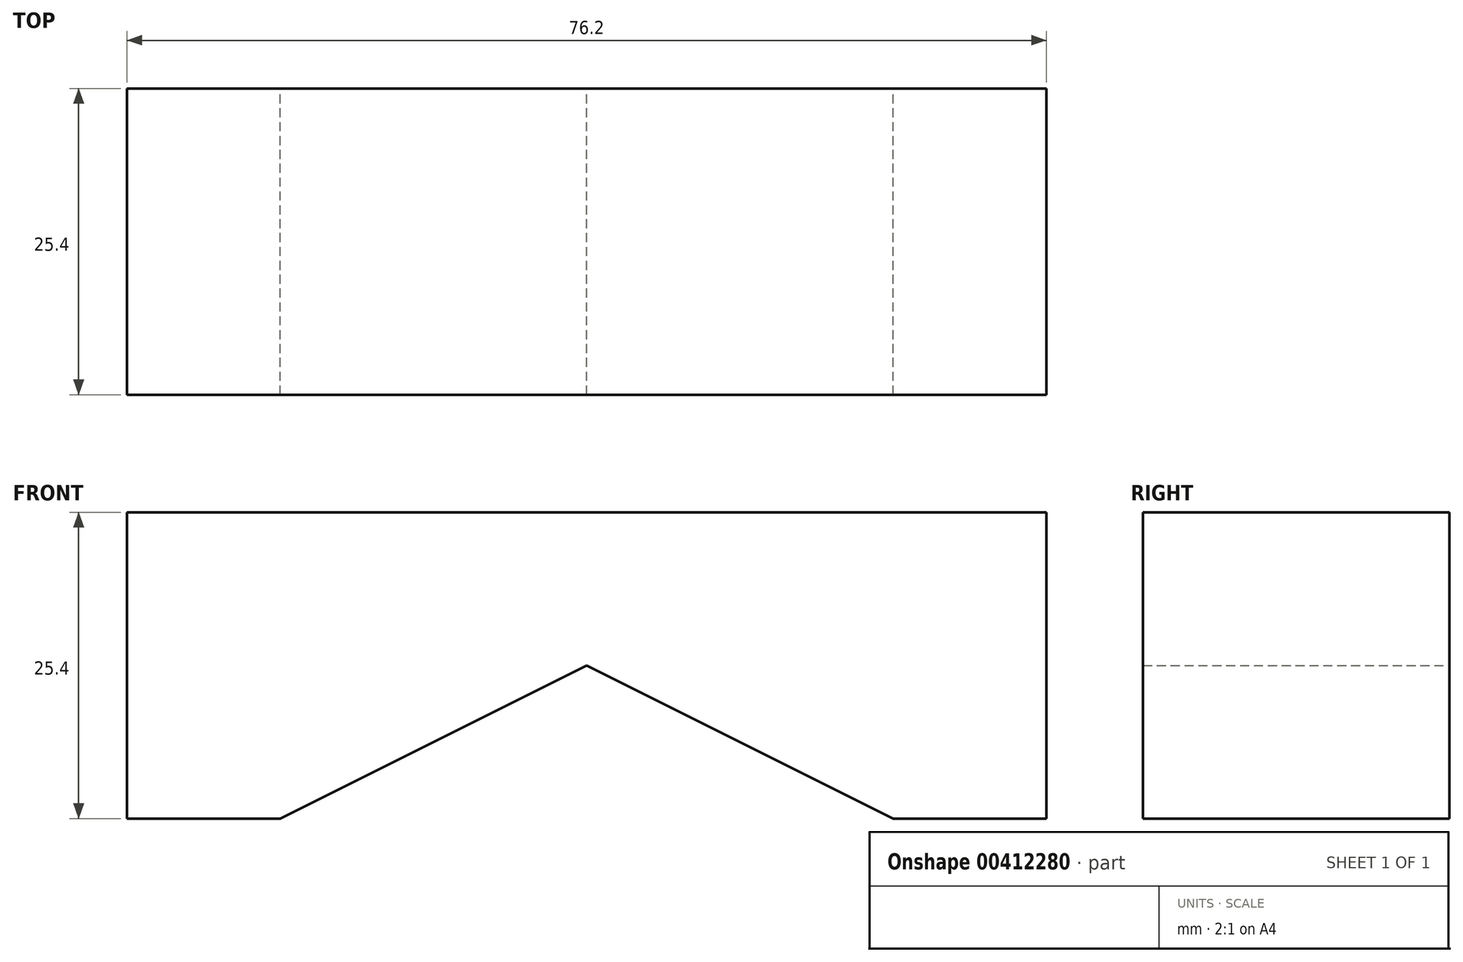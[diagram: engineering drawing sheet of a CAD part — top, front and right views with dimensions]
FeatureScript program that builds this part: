
annotation { "Feature Type Name" : "Feature", "Feature Type Description" : "" }
export const myFeature = defineFeature(function(context is Context, id is Id, definition is map)
    precondition{}
    {
        {
            var Q0;
            Q0=qCreatedBy(makeId("Front.planeOp"),FACE);
            var sketch = newSketch(context, id + "F0", { "sketchPlane" : qUnion([Q0])});
            skLineSegment(sketch, "E0", {"start": v(0, 0) * mm, "end": v(-25.4, 0) * mm, "construction": true});
            skLineSegment(sketch, "E1", {"start": v(-25.4, 0) * mm, "end": v(-38.1, 0) * mm});
            skLineSegment(sketch, "E2", {"start": v(-38.1, 0) * mm, "end": v(-38.1, 25.4) * mm});
            skLineSegment(sketch, "E3", {"start": v(-38.1, 25.4) * mm, "end": v(38.1, 25.4) * mm});
            skLineSegment(sketch, "E4", {"start": v(38.1, 25.4) * mm, "end": v(38.1, 0) * mm});
            skLineSegment(sketch, "E5", {"start": v(38.1, 0) * mm, "end": v(25.4, 0) * mm});
            skLineSegment(sketch, "E6", {"start": v(0, 0) * mm, "end": v(0, 12.7) * mm, "construction": true});
            skLineSegment(sketch, "E7", {"start": v(25.4, 0) * mm, "end": v(0, 12.7) * mm});
            skLineSegment(sketch, "E8", {"start": v(-25.4, 0) * mm, "end": v(0, 12.7) * mm});
            skSolve(sketch);
        }
        {
            var Q0;
            Q0=makeQuery(id+"F0.imprint","IMPRINT",FACE,{"disambiguationData":[TD([[makeQuery(id+"F0.imprint","IMPRINT",EDGE,{"derivedFrom":sQuery(id+"F0.wireOp",EDGE,"E1")}),-1.0]])]});
            extrude(context, id + "F1", {"entities" : qUnion([Q0]), "depth" : 25.4 * mm});
        }
    });
